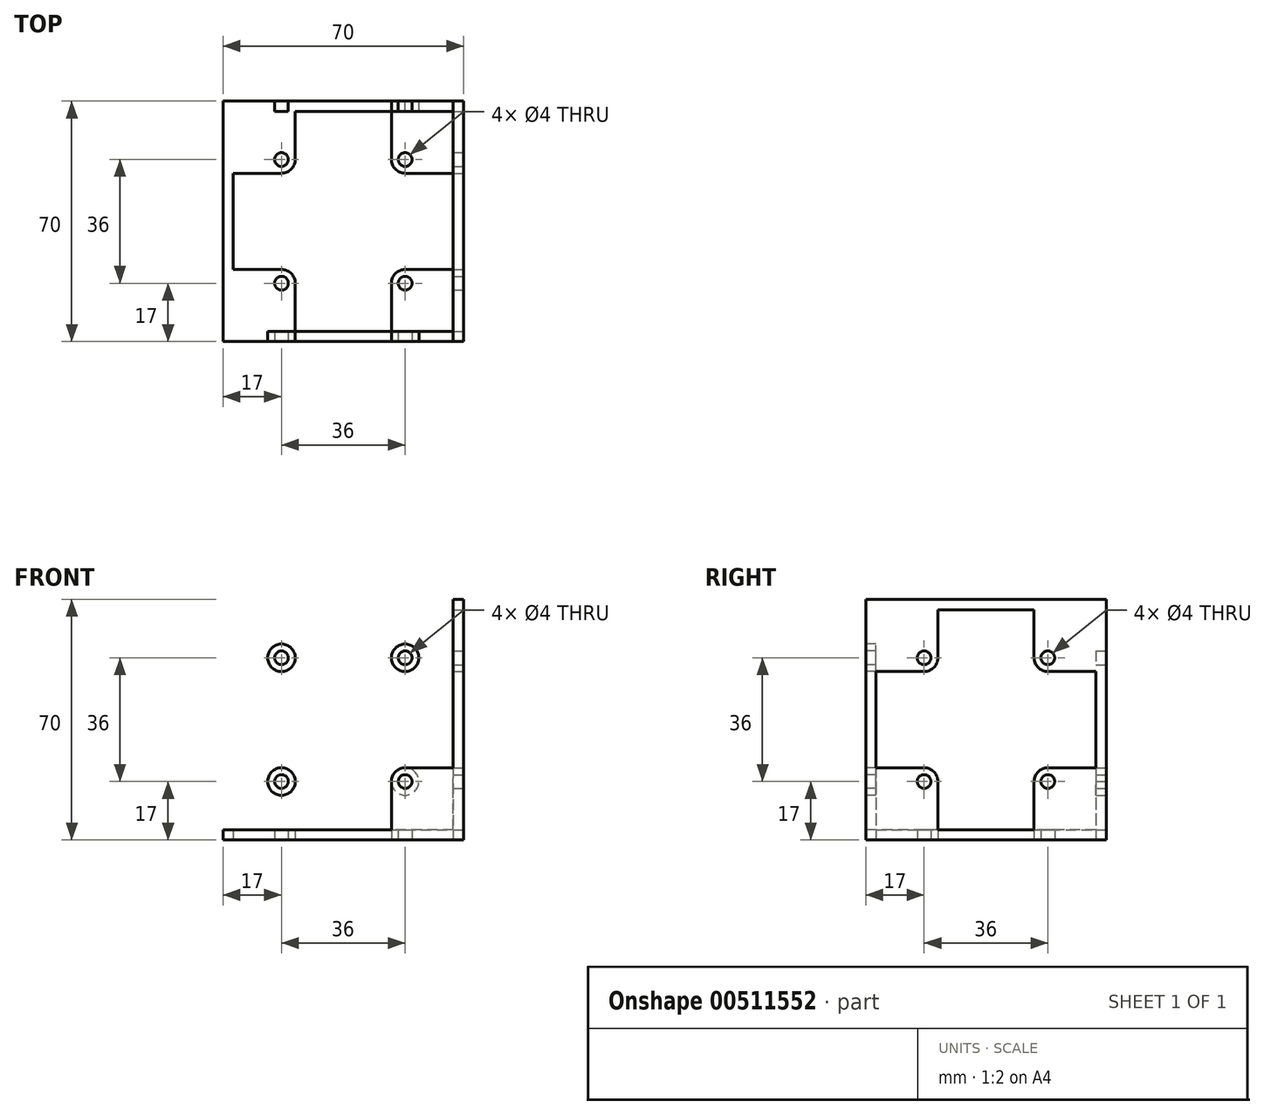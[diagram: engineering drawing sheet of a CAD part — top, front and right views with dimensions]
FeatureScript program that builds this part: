
annotation { "Feature Type Name" : "Feature", "Feature Type Description" : "" }
export const myFeature = defineFeature(function(context is Context, id is Id, definition is map)
    precondition{}
    {
        {
            var Q0;
            Q0=qCreatedBy(makeId("Front.planeOp"),FACE);
            var sketch = newSketch(context, id + "F0", { "sketchPlane" : qUnion([Q0])});
            skLineSegment(sketch, "E0", {"start": v(-35, 0) * mm, "end": v(-35, 35) * mm});
            skLineSegment(sketch, "E1", {"start": v(-35, 35) * mm, "end": v(35, 35) * mm});
            skLineSegment(sketch, "E2", {"start": v(35, 35) * mm, "end": v(35, 0) * mm});
            skLineSegment(sketch, "E3", {"start": v(35, 0) * mm, "end": v(35, -35) * mm});
            skLineSegment(sketch, "E4", {"start": v(35, -35) * mm, "end": v(-35, -35) * mm});
            skLineSegment(sketch, "E5", {"start": v(-35, -35) * mm, "end": v(-35, 0) * mm});
            skLineSegment(sketch, "E6", {"start": v(-32, 32) * mm, "end": v(32, 32) * mm});
            skLineSegment(sketch, "E7", {"start": v(32, 32) * mm, "end": v(32, -32) * mm});
            skLineSegment(sketch, "E8", {"start": v(32, -32) * mm, "end": v(-32, -32) * mm});
            skLineSegment(sketch, "E9", {"start": v(-32, -32) * mm, "end": v(-32, 32) * mm});
            skLineSegment(sketch, "E10", {"start": v(-18, -14) * mm, "end": v(-32, -14) * mm});
            skLineSegment(sketch, "E11", {"start": v(32, 14) * mm, "end": v(18, 14) * mm});
            skLineSegment(sketch, "E12", {"start": v(18, -14) * mm, "end": v(32, -14) * mm});
            skLineSegment(sketch, "E13", {"start": v(14, 32) * mm, "end": v(14, 18) * mm});
            skLineSegment(sketch, "E14", {"start": v(-14, -18) * mm, "end": v(-14, -32) * mm});
            skLineSegment(sketch, "E15", {"start": v(14, -18) * mm, "end": v(14, -32) * mm});
            skLineSegment(sketch, "E16", {"start": v(-14, 18) * mm, "end": v(-14, 32) * mm});
            skLineSegment(sketch, "E17", {"start": v(-18, 14) * mm, "end": v(-32, 14) * mm});
            skCircle(sketch, "E18", {"center": v(-18, 18) * mm, "radius": 2 * mm});
            skCircle(sketch, "E19", {"center": v(-18, 18) * mm, "radius": 4 * mm});
            skPoint(sketch, "E20.visualSharp", {"position": v(-14, 14) * mm});
            skArc(sketch, "E20.filletArc", {"start": v(-18, 14) * mm, "mid": v(-15.17, 15.17) * mm, "end": v(-14, 18) * mm});
            skCircle(sketch, "E21", {"center": v(18, 18) * mm, "radius": 2 * mm});
            skCircle(sketch, "E22", {"center": v(18, 18) * mm, "radius": 4 * mm});
            skCircle(sketch, "E23", {"center": v(-18, -18) * mm, "radius": 2 * mm});
            skCircle(sketch, "E24", {"center": v(-18, -18) * mm, "radius": 4 * mm});
            skCircle(sketch, "E25", {"center": v(18, -18) * mm, "radius": 2 * mm});
            skCircle(sketch, "E26", {"center": v(18, -18) * mm, "radius": 4 * mm});
            skLineSegment(sketch, "E27", {"start": v(-32, 32) * mm, "end": v(-35, 32) * mm});
            skLineSegment(sketch, "E28", {"start": v(-35, 32) * mm, "end": v(-32, 32) * mm});
            skLineSegment(sketch, "E29", {"start": v(32, 32) * mm, "end": v(32, 35) * mm});
            skLineSegment(sketch, "E30", {"start": v(32, 32) * mm, "end": v(35, 32) * mm});
            skLineSegment(sketch, "E31", {"start": v(-35, -32) * mm, "end": v(-32, -32) * mm});
            skLineSegment(sketch, "E32", {"start": v(-32, -32) * mm, "end": v(-32, -35) * mm});
            skLineSegment(sketch, "E33", {"start": v(32, -32) * mm, "end": v(32, -35) * mm});
            skLineSegment(sketch, "E34", {"start": v(32, -32) * mm, "end": v(35, -32) * mm});
            skPoint(sketch, "E35.visualSharp", {"position": v(14, 14) * mm});
            skArc(sketch, "E35.filletArc", {"start": v(14, 18) * mm, "mid": v(15.17, 15.17) * mm, "end": v(18, 14) * mm});
            skPoint(sketch, "E36.visualSharp", {"position": v(14, -14) * mm});
            skArc(sketch, "E36.filletArc", {"start": v(18, -14) * mm, "mid": v(15.17, -15.17) * mm, "end": v(14, -18) * mm});
            skPoint(sketch, "E37.visualSharp", {"position": v(-14, -14) * mm});
            skArc(sketch, "E37.filletArc", {"start": v(-14, -18) * mm, "mid": v(-15.17, -15.17) * mm, "end": v(-18, -14) * mm});
            skCircle(sketch, "E38", {"center": v(-18, 18) * mm, "radius": 6 * mm});
            skSolve(sketch);
        }
        {
            var Q0;
            {var subQ3=sQuery(id+"F0.wireOp",EDGE,"E28");Q0=makeQuery(id+"F0.imprint","IMPRINT",FACE,{"disambiguationData":[TD([[makeQuery(id+"F0.imprint","IMPRINT",EDGE,{"derivedFrom":subQ3}),1.0]])]});}
            var Q1;
            {var subQ7=sQuery(id+"F0.wireOp",EDGE,"E30");Q1=makeQuery(id+"F0.imprint","IMPRINT",FACE,{"disambiguationData":[TD([[makeQuery(id+"F0.imprint","IMPRINT",EDGE,{"derivedFrom":subQ7}),-1.0]])]});}
            var Q2;
            {var subQ3=sQuery(id+"F0.wireOp",EDGE,"E29");Q2=makeQuery(id+"F0.imprint","IMPRINT",FACE,{"disambiguationData":[TD([[makeQuery(id+"F0.imprint","IMPRINT",EDGE,{"derivedFrom":subQ3}),-1.0]])]});}
            var Q3;
            {var subQ7=sQuery(id+"F0.wireOp",EDGE,"E28");Q3=makeQuery(id+"F0.imprint","IMPRINT",FACE,{"disambiguationData":[TD([[makeQuery(id+"F0.imprint","IMPRINT",EDGE,{"derivedFrom":subQ7}),-1.0]])]});}
            var Q4;
            {var subQ0=sQuery(id+"F0.wireOp",EDGE,"E32");Q4=makeQuery(id+"F0.imprint","IMPRINT",FACE,{"disambiguationData":[TD([[makeQuery(id+"F0.imprint","IMPRINT",EDGE,{"derivedFrom":subQ0}),1.0]])]});}
            var Q5;
            {var subQ4=sQuery(id+"F0.wireOp",EDGE,"E31");Q5=makeQuery(id+"F0.imprint","IMPRINT",FACE,{"disambiguationData":[TD([[makeQuery(id+"F0.imprint","IMPRINT",EDGE,{"derivedFrom":subQ4}),-1.0]])]});}
            var Q6;
            {var subQ4=sQuery(id+"F0.wireOp",EDGE,"E33");Q6=makeQuery(id+"F0.imprint","IMPRINT",FACE,{"disambiguationData":[TD([[makeQuery(id+"F0.imprint","IMPRINT",EDGE,{"derivedFrom":subQ4}),1.0]])]});}
            extrude(context, id + "F1", {"entities" : qUnion([Q0, Q1, Q2, Q3, Q4, Q5, Q6]), "endBound" : BoundingType.SYMMETRIC, "depth" : 70 * mm, "offsetDistance" : 25 * mm});
        }
        {
            var Q0;
            Q0=makeQuery(id+"F1.opExtrude","CAP_FACE",FACE,{"disambiguationData":[OSD([sQuery(id+"F0.wireOp",EDGE,"E0"),sQuery(id+"F0.wireOp",EDGE,"E1"),sQuery(id+"F0.wireOp",EDGE,"E2"),sQuery(id+"F0.wireOp",EDGE,"E3"),sQuery(id+"F0.wireOp",EDGE,"E4"),sQuery(id+"F0.wireOp",EDGE,"E5"),sQuery(id+"F0.wireOp",EDGE,"E6"),sQuery(id+"F0.wireOp",EDGE,"E7"),sQuery(id+"F0.wireOp",EDGE,"E8"),sQuery(id+"F0.wireOp",EDGE,"E9")])],"isStart":false});
            var sketch = newSketch(context, id + "F2", { "sketchPlane" : qUnion([Q0])});
            skLineSegment(sketch, "E39.0", {"start": v(-18, 14) * mm, "end": v(-32, 14) * mm});
            skLineSegment(sketch, "E39.1", {"start": v(-14, 18) * mm, "end": v(-14, 32) * mm});
            skArc(sketch, "E39.2", {"start": v(-18, 14) * mm, "mid": v(-15.17, 15.17) * mm, "end": v(-14, 18) * mm});
            skCircle(sketch, "E39.3", {"center": v(-18, 18) * mm, "radius": 2 * mm});
            skCircle(sketch, "E39.4", {"center": v(-18, 18) * mm, "radius": 4 * mm});
            skLineSegment(sketch, "E39.5", {"start": v(14, 32) * mm, "end": v(14, 18) * mm});
            skCircle(sketch, "E39.6", {"center": v(18, 18) * mm, "radius": 4 * mm});
            skLineSegment(sketch, "E39.7", {"start": v(32, 14) * mm, "end": v(18, 14) * mm});
            skLineSegment(sketch, "E39.8", {"start": v(18, -14) * mm, "end": v(32, -14) * mm});
            skCircle(sketch, "E39.9", {"center": v(18, -18) * mm, "radius": 4 * mm});
            skCircle(sketch, "E39.10", {"center": v(18, -18) * mm, "radius": 2 * mm});
            skLineSegment(sketch, "E39.11", {"start": v(14, -18) * mm, "end": v(14, -32) * mm});
            skLineSegment(sketch, "E39.12", {"start": v(-14, -18) * mm, "end": v(-14, -32) * mm});
            skCircle(sketch, "E39.13", {"center": v(-18, -18) * mm, "radius": 4 * mm});
            skLineSegment(sketch, "E39.14", {"start": v(-18, -14) * mm, "end": v(-32, -14) * mm});
            skCircle(sketch, "E39.15", {"center": v(-18, -18) * mm, "radius": 2 * mm});
            skCircle(sketch, "E40.0", {"center": v(18, 18) * mm, "radius": 2 * mm});
            skSolve(sketch);
        }
        {
            var Q0;
            {var subQ5=sQuery(id+"F2.wireOp",EDGE,"E39.0");Q0=makeQuery(id+"F2.imprint","IMPRINT",FACE,{"disambiguationData":[TD([[makeQuery(id+"F2.imprint","IMPRINT",EDGE,{"derivedFrom":subQ5}),-1.0]])]});}
            var Q1;
            Q1=makeQuery(id+"F2.imprint","IMPRINT",FACE,{"disambiguationData":[TD([[makeQuery(id+"F2.imprint","IMPRINT",EDGE,{"derivedFrom":sQuery(id+"F2.wireOp",EDGE,"E39.3")}),-1.0]])]});
            var Q2;
            Q2=makeQuery(id+"F2.imprint","IMPRINT",FACE,{"disambiguationData":[TD([[makeQuery(id+"F2.imprint","IMPRINT",EDGE,{"derivedFrom":sQuery(id+"F2.wireOp",EDGE,"E40.0")}),-1.0]])]});
            var Q3;
            {var subQ2=sQuery(id+"F2.wireOp",EDGE,"E39.5");Q3=makeQuery(id+"F2.imprint","IMPRINT",FACE,{"disambiguationData":[TD([[makeQuery(id+"F2.imprint","IMPRINT",EDGE,{"derivedFrom":subQ2}),1.0]])]});}
            var Q4;
            {var subQ3=sQuery(id+"F2.wireOp",EDGE,"E39.8");Q4=makeQuery(id+"F2.imprint","IMPRINT",FACE,{"disambiguationData":[TD([[makeQuery(id+"F2.imprint","IMPRINT",EDGE,{"derivedFrom":subQ3}),-1.0]])]});}
            var Q5;
            Q5=makeQuery(id+"F2.imprint","IMPRINT",FACE,{"disambiguationData":[TD([[makeQuery(id+"F2.imprint","IMPRINT",EDGE,{"derivedFrom":sQuery(id+"F2.wireOp",EDGE,"E39.10")}),-1.0]])]});
            var Q6;
            Q6=makeQuery(id+"F2.imprint","IMPRINT",FACE,{"disambiguationData":[TD([[makeQuery(id+"F2.imprint","IMPRINT",EDGE,{"derivedFrom":sQuery(id+"F2.wireOp",EDGE,"E39.15")}),-1.0]])]});
            var Q7;
            {var subQ4=sQuery(id+"F2.wireOp",EDGE,"E39.12");Q7=makeQuery(id+"F2.imprint","IMPRINT",FACE,{"disambiguationData":[TD([[makeQuery(id+"F2.imprint","IMPRINT",EDGE,{"derivedFrom":subQ4}),-1.0]])]});}
            extrude(context, id + "F3", {"entities" : qUnion([Q0, Q1, Q2, Q3, Q4, Q5, Q6, Q7]), "operationType" : NewBodyOperationType.ADD, "oppositeDirection" : true, "depth" : 3 * mm, "offsetDistance" : 25 * mm});
        }
        {
            var Q0;
            Q0=makeQuery(id+"F1.opExtrude","CAP_FACE",FACE,{"disambiguationData":[OSD([sQuery(id+"F0.wireOp",EDGE,"E0"),sQuery(id+"F0.wireOp",EDGE,"E1"),sQuery(id+"F0.wireOp",EDGE,"E2"),sQuery(id+"F0.wireOp",EDGE,"E3"),sQuery(id+"F0.wireOp",EDGE,"E4"),sQuery(id+"F0.wireOp",EDGE,"E5"),sQuery(id+"F0.wireOp",EDGE,"E6"),sQuery(id+"F0.wireOp",EDGE,"E7"),sQuery(id+"F0.wireOp",EDGE,"E8"),sQuery(id+"F0.wireOp",EDGE,"E9")])],"isStart":true});
            var sketch = newSketch(context, id + "F4", { "sketchPlane" : qUnion([Q0])});
            skLineSegment(sketch, "E41.0", {"start": v(14, 18) * mm, "end": v(14, 32) * mm});
            skArc(sketch, "E41.1", {"start": v(18, 14) * mm, "mid": v(15.17, 15.17) * mm, "end": v(14, 18) * mm});
            skLineSegment(sketch, "E41.2", {"start": v(18, 14) * mm, "end": v(32, 14) * mm});
            skCircle(sketch, "E41.3", {"center": v(18, 18) * mm, "radius": 2 * mm});
            skCircle(sketch, "E41.4", {"center": v(-18, 18) * mm, "radius": 2 * mm});
            skLineSegment(sketch, "E41.5", {"start": v(-32, 14) * mm, "end": v(-18, 14) * mm});
            skLineSegment(sketch, "E41.6", {"start": v(-14, 32) * mm, "end": v(-14, 18) * mm});
            skCircle(sketch, "E41.7", {"center": v(-18, 18) * mm, "radius": 4 * mm});
            skCircle(sketch, "E41.8", {"center": v(18, 18) * mm, "radius": 4 * mm});
            skLineSegment(sketch, "E41.9", {"start": v(-18, -14) * mm, "end": v(-32, -14) * mm});
            skArc(sketch, "E41.10", {"start": v(-18, -14) * mm, "mid": v(-15.17, -15.17) * mm, "end": v(-14, -18) * mm});
            skCircle(sketch, "E41.11", {"center": v(-18, -18) * mm, "radius": 4 * mm});
            skArc(sketch, "E41.12", {"start": v(14, -18) * mm, "mid": v(15.17, -15.17) * mm, "end": v(18, -14) * mm});
            skLineSegment(sketch, "E41.13", {"start": v(18, -14) * mm, "end": v(32, -14) * mm});
            skCircle(sketch, "E41.14", {"center": v(18, -18) * mm, "radius": 4 * mm});
            skCircle(sketch, "E41.15", {"center": v(18, -18) * mm, "radius": 2 * mm});
            skLineSegment(sketch, "E41.16", {"start": v(14, -18) * mm, "end": v(14, -32) * mm});
            skLineSegment(sketch, "E41.17", {"start": v(-14, -18) * mm, "end": v(-14, -32) * mm});
            skCircle(sketch, "E41.18", {"center": v(-18, -18) * mm, "radius": 2 * mm});
            skSolve(sketch);
        }
        {
            var Q0;
            {var subQ1=sQuery(id+"F4.wireOp",EDGE,"E41.5");Q0=makeQuery(id+"F4.imprint","IMPRINT",FACE,{"disambiguationData":[TD([[makeQuery(id+"F4.imprint","IMPRINT",EDGE,{"derivedFrom":subQ1}),1.0]])]});}
            var Q1;
            Q1=makeQuery(id+"F4.imprint","IMPRINT",FACE,{"disambiguationData":[TD([[makeQuery(id+"F4.imprint","IMPRINT",EDGE,{"derivedFrom":sQuery(id+"F4.wireOp",EDGE,"E41.4")}),1.0]])]});
            var Q2;
            {var subQ3=sQuery(id+"F4.wireOp",EDGE,"E41.0");Q2=makeQuery(id+"F4.imprint","IMPRINT",FACE,{"disambiguationData":[TD([[makeQuery(id+"F4.imprint","IMPRINT",EDGE,{"derivedFrom":subQ3}),-1.0]])]});}
            var Q3;
            Q3=makeQuery(id+"F4.imprint","IMPRINT",FACE,{"disambiguationData":[TD([[makeQuery(id+"F4.imprint","IMPRINT",EDGE,{"derivedFrom":sQuery(id+"F4.wireOp",EDGE,"E41.3")}),1.0]])]});
            var Q4;
            {var subQ5=sQuery(id+"F4.wireOp",EDGE,"E41.13");Q4=makeQuery(id+"F4.imprint","IMPRINT",FACE,{"disambiguationData":[TD([[makeQuery(id+"F4.imprint","IMPRINT",EDGE,{"derivedFrom":subQ5}),-1.0]])]});}
            var Q5;
            Q5=makeQuery(id+"F4.imprint","IMPRINT",FACE,{"disambiguationData":[TD([[makeQuery(id+"F4.imprint","IMPRINT",EDGE,{"derivedFrom":sQuery(id+"F4.wireOp",EDGE,"E41.15")}),1.0]])]});
            var Q6;
            Q6=makeQuery(id+"F4.imprint","IMPRINT",FACE,{"disambiguationData":[TD([[makeQuery(id+"F4.imprint","IMPRINT",EDGE,{"derivedFrom":sQuery(id+"F4.wireOp",EDGE,"E41.18")}),1.0]])]});
            var Q7;
            {var subQ3=sQuery(id+"F4.wireOp",EDGE,"E41.9");Q7=makeQuery(id+"F4.imprint","IMPRINT",FACE,{"disambiguationData":[TD([[makeQuery(id+"F4.imprint","IMPRINT",EDGE,{"derivedFrom":subQ3}),1.0]])]});}
            extrude(context, id + "F5", {"entities" : qUnion([Q0, Q1, Q2, Q3, Q4, Q5, Q6, Q7]), "operationType" : NewBodyOperationType.ADD, "oppositeDirection" : true, "depth" : 3 * mm, "offsetDistance" : 25 * mm});
        }
        {
            var Q0;
            Q0=makeQuery(id+"F1.opExtrude","SWEPT_FACE",FACE,{"disambiguationData":[OSD([sQuery(id+"F0.wireOp",EDGE,"E2"),sQuery(id+"F0.wireOp",EDGE,"E3")])]});
            var sketch = newSketch(context, id + "F6", { "sketchPlane" : qUnion([Q0])});
            skLineSegment(sketch, "E42", {"start": v(-35, 32) * mm, "end": v(35, 32) * mm});
            skLineSegment(sketch, "E43", {"start": v(-32, 35) * mm, "end": v(-32, -35) * mm});
            skLineSegment(sketch, "E44", {"start": v(32, 35) * mm, "end": v(32, -35) * mm});
            skLineSegment(sketch, "E45", {"start": v(35, -32) * mm, "end": v(-35, -32) * mm});
            skLineSegment(sketch, "E46", {"start": v(-14, 32) * mm, "end": v(-14, 18) * mm});
            skLineSegment(sketch, "E47", {"start": v(-18, 14) * mm, "end": v(-32, 14) * mm});
            skLineSegment(sketch, "E48", {"start": v(-32, -14) * mm, "end": v(-18, -14) * mm});
            skLineSegment(sketch, "E49", {"start": v(-14, -18) * mm, "end": v(-14, -32) * mm});
            skLineSegment(sketch, "E50", {"start": v(14, -32) * mm, "end": v(14, -18) * mm});
            skLineSegment(sketch, "E51", {"start": v(18, -14) * mm, "end": v(32, -14) * mm});
            skLineSegment(sketch, "E52", {"start": v(14, 32) * mm, "end": v(14, 18) * mm});
            skLineSegment(sketch, "E53", {"start": v(18, 14) * mm, "end": v(32, 14) * mm});
            skCircle(sketch, "E54", {"center": v(-18, 18) * mm, "radius": 2 * mm});
            skCircle(sketch, "E55", {"center": v(-18, 18) * mm, "radius": 4 * mm});
            skCircle(sketch, "E56", {"center": v(18, 18) * mm, "radius": 2 * mm});
            skCircle(sketch, "E57", {"center": v(18, 18) * mm, "radius": 4 * mm});
            skCircle(sketch, "E58", {"center": v(18, -18) * mm, "radius": 2 * mm});
            skCircle(sketch, "E59", {"center": v(18, -18) * mm, "radius": 4 * mm});
            skCircle(sketch, "E60", {"center": v(-18, -18) * mm, "radius": 2 * mm});
            skCircle(sketch, "E61", {"center": v(-18, -18) * mm, "radius": 4 * mm});
            skPoint(sketch, "E62.visualSharp", {"position": v(-14, 14) * mm});
            skArc(sketch, "E62.filletArc", {"start": v(-18, 14) * mm, "mid": v(-15.17, 15.17) * mm, "end": v(-14, 18) * mm});
            skPoint(sketch, "E63.visualSharp", {"position": v(14, 14) * mm});
            skArc(sketch, "E63.filletArc", {"start": v(14, 18) * mm, "mid": v(15.17, 15.17) * mm, "end": v(18, 14) * mm});
            skPoint(sketch, "E64.visualSharp", {"position": v(14, -14) * mm});
            skArc(sketch, "E64.filletArc", {"start": v(18, -14) * mm, "mid": v(15.17, -15.17) * mm, "end": v(14, -18) * mm});
            skPoint(sketch, "E65.visualSharp", {"position": v(-14, -14) * mm});
            skArc(sketch, "E65.filletArc", {"start": v(-14, -18) * mm, "mid": v(-15.17, -15.17) * mm, "end": v(-18, -14) * mm});
            skSolve(sketch);
        }
        {
            var Q0;
            {var subQ1=sQuery(id+"F6.wireOp",EDGE,"E46");Q0=makeQuery(id+"F6.imprint","IMPRINT",FACE,{"disambiguationData":[TD([[makeQuery(id+"F6.imprint","IMPRINT",EDGE,{"derivedFrom":subQ1}),1.0]])]});}
            var Q1;
            Q1=makeQuery(id+"F6.imprint","IMPRINT",FACE,{"disambiguationData":[TD([[makeQuery(id+"F6.imprint","IMPRINT",EDGE,{"derivedFrom":sQuery(id+"F6.wireOp",EDGE,"E54")}),1.0]])]});
            var Q2;
            Q2=makeQuery(id+"F6.imprint","IMPRINT",FACE,{"disambiguationData":[TD([[makeQuery(id+"F6.imprint","IMPRINT",EDGE,{"derivedFrom":sQuery(id+"F6.wireOp",EDGE,"E56")}),1.0]])]});
            var Q3;
            Q3=makeQuery(id+"F6.imprint","IMPRINT",FACE,{"disambiguationData":[TD([[makeQuery(id+"F6.imprint","IMPRINT",EDGE,{"derivedFrom":sQuery(id+"F6.wireOp",EDGE,"E58")}),1.0]])]});
            var Q4;
            Q4=makeQuery(id+"F6.imprint","IMPRINT",FACE,{"disambiguationData":[TD([[makeQuery(id+"F6.imprint","IMPRINT",EDGE,{"derivedFrom":sQuery(id+"F6.wireOp",EDGE,"E60")}),1.0]])]});
            extrude(context, id + "F7", {"entities" : qUnion([Q0, Q1, Q2, Q3, Q4]), "operationType" : NewBodyOperationType.REMOVE, "oppositeDirection" : true, "depth" : 3 * mm, "offsetDistance" : 25 * mm});
        }
        {
            var Q0;
            Q0=makeQuery(id+"F1.opExtrude","SWEPT_FACE",FACE,{"disambiguationData":[OSD([sQuery(id+"F0.wireOp",EDGE,"E0"),sQuery(id+"F0.wireOp",EDGE,"E5")])]});
            var sketch = newSketch(context, id + "F8", { "sketchPlane" : qUnion([Q0])});
            skLineSegment(sketch, "E66.0", {"start": v(-18, 14) * mm, "end": v(-32, 14) * mm});
            skLineSegment(sketch, "E66.1", {"start": v(-14, 32) * mm, "end": v(-14, 18) * mm});
            skCircle(sketch, "E66.2", {"center": v(-18, 18) * mm, "radius": 4 * mm});
            skCircle(sketch, "E66.3", {"center": v(-18, 18) * mm, "radius": 2 * mm});
            skLineSegment(sketch, "E66.4", {"start": v(18, 14) * mm, "end": v(32, 14) * mm});
            skCircle(sketch, "E66.5", {"center": v(18, 18) * mm, "radius": 4 * mm});
            skLineSegment(sketch, "E66.6", {"start": v(14, 32) * mm, "end": v(14, 18) * mm});
            skCircle(sketch, "E66.7", {"center": v(18, 18) * mm, "radius": 2 * mm});
            skCircle(sketch, "E66.8", {"center": v(18, -18) * mm, "radius": 4 * mm});
            skLineSegment(sketch, "E66.9", {"start": v(32, -14) * mm, "end": v(18, -14) * mm});
            skCircle(sketch, "E66.10", {"center": v(18, -18) * mm, "radius": 2 * mm});
            skLineSegment(sketch, "E66.11", {"start": v(14, -18) * mm, "end": v(14, -32) * mm});
            skLineSegment(sketch, "E66.12", {"start": v(-14, -32) * mm, "end": v(-14, -18) * mm});
            skCircle(sketch, "E66.13", {"center": v(-18, -18) * mm, "radius": 4 * mm});
            skCircle(sketch, "E66.14", {"center": v(-18, -18) * mm, "radius": 2 * mm});
            skLineSegment(sketch, "E66.15", {"start": v(-18, -14) * mm, "end": v(-32, -14) * mm});
            skLineSegment(sketch, "E67", {"start": v(-14, 32) * mm, "end": v(14, 32) * mm});
            skLineSegment(sketch, "E68", {"start": v(-32, 14) * mm, "end": v(-32, -14) * mm});
            skLineSegment(sketch, "E69", {"start": v(-14, -32) * mm, "end": v(14, -32) * mm});
            skLineSegment(sketch, "E70", {"start": v(32, -14) * mm, "end": v(32, 14) * mm});
            skSolve(sketch);
        }
        {
            var Q0;
            {var subQ7=sQuery(id+"F8.wireOp",EDGE,"E66.0");Q0=makeQuery(id+"F8.imprint","IMPRINT",FACE,{"disambiguationData":[TD([[makeQuery(id+"F8.imprint","IMPRINT",EDGE,{"derivedFrom":subQ7}),1.0]])]});}
            var Q1;
            Q1=makeQuery(id+"F8.imprint","IMPRINT",FACE,{"disambiguationData":[TD([[makeQuery(id+"F8.imprint","IMPRINT",EDGE,{"derivedFrom":sQuery(id+"F8.wireOp",EDGE,"E66.3")}),-1.0]])]});
            var Q2;
            Q2=makeQuery(id+"F8.imprint","IMPRINT",FACE,{"disambiguationData":[TD([[makeQuery(id+"F8.imprint","IMPRINT",EDGE,{"derivedFrom":sQuery(id+"F8.wireOp",EDGE,"E66.7")}),-1.0]])]});
            var Q3;
            Q3=makeQuery(id+"F8.imprint","IMPRINT",FACE,{"disambiguationData":[TD([[makeQuery(id+"F8.imprint","IMPRINT",EDGE,{"derivedFrom":sQuery(id+"F8.wireOp",EDGE,"E66.10")}),-1.0]])]});
            var Q4;
            Q4=makeQuery(id+"F8.imprint","IMPRINT",FACE,{"disambiguationData":[TD([[makeQuery(id+"F8.imprint","IMPRINT",EDGE,{"derivedFrom":sQuery(id+"F8.wireOp",EDGE,"E66.14")}),-1.0]])]});
            extrude(context, id + "F9", {"entities" : qUnion([Q0, Q1, Q2, Q3, Q4]), "operationType" : NewBodyOperationType.REMOVE, "oppositeDirection" : true, "depth" : 3 * mm, "offsetDistance" : 25 * mm});
        }
        {
            var Q0;
            Q0=makeQuery(id+"F1.opExtrude","SWEPT_FACE",FACE,{"disambiguationData":[OSD([sQuery(id+"F0.wireOp",EDGE,"E1")])]});
            var sketch = newSketch(context, id + "F10", { "sketchPlane" : qUnion([Q0])});
            skLineSegment(sketch, "E71", {"start": v(-35, 32) * mm, "end": v(35, 32) * mm});
            skLineSegment(sketch, "E72", {"start": v(32, 35) * mm, "end": v(32, -35) * mm});
            skLineSegment(sketch, "E73", {"start": v(-35, -32) * mm, "end": v(35, -32) * mm});
            skLineSegment(sketch, "E74", {"start": v(-32, 35) * mm, "end": v(-32, -35) * mm});
            skLineSegment(sketch, "E75", {"start": v(-14, 32) * mm, "end": v(-14, 18) * mm});
            skLineSegment(sketch, "E76", {"start": v(-18, 14) * mm, "end": v(-32, 14) * mm});
            skLineSegment(sketch, "E77", {"start": v(14, 32) * mm, "end": v(14, 18) * mm});
            skLineSegment(sketch, "E78", {"start": v(18, 14) * mm, "end": v(32, 14) * mm});
            skLineSegment(sketch, "E79", {"start": v(-32, -14) * mm, "end": v(-18, -14) * mm});
            skLineSegment(sketch, "E80", {"start": v(-14, -18) * mm, "end": v(-14, -32) * mm});
            skLineSegment(sketch, "E81", {"start": v(32, -14) * mm, "end": v(18, -14) * mm});
            skLineSegment(sketch, "E82", {"start": v(14, -18) * mm, "end": v(14, -32) * mm});
            skCircle(sketch, "E83", {"center": v(-18, 18) * mm, "radius": 2 * mm});
            skCircle(sketch, "E84", {"center": v(-18, 18) * mm, "radius": 4 * mm});
            skCircle(sketch, "E85", {"center": v(18, 18) * mm, "radius": 2 * mm});
            skCircle(sketch, "E86", {"center": v(18, 18) * mm, "radius": 4 * mm});
            skCircle(sketch, "E87", {"center": v(-18, -18) * mm, "radius": 2 * mm});
            skCircle(sketch, "E88", {"center": v(-18, -18) * mm, "radius": 4 * mm});
            skCircle(sketch, "E89", {"center": v(18, -18) * mm, "radius": 2 * mm});
            skCircle(sketch, "E90", {"center": v(18, -18) * mm, "radius": 4 * mm});
            skPoint(sketch, "E91.visualSharp", {"position": v(-14, 14) * mm});
            skArc(sketch, "E91.filletArc", {"start": v(-18, 14) * mm, "mid": v(-15.17, 15.17) * mm, "end": v(-14, 18) * mm});
            skPoint(sketch, "E92.visualSharp", {"position": v(14, 14) * mm});
            skArc(sketch, "E92.filletArc", {"start": v(14, 18) * mm, "mid": v(15.17, 15.17) * mm, "end": v(18, 14) * mm});
            skPoint(sketch, "E93.visualSharp", {"position": v(14, -14) * mm});
            skArc(sketch, "E93.filletArc", {"start": v(18, -14) * mm, "mid": v(15.17, -15.17) * mm, "end": v(14, -18) * mm});
            skPoint(sketch, "E94.visualSharp", {"position": v(-14, -14) * mm});
            skArc(sketch, "E94.filletArc", {"start": v(-14, -18) * mm, "mid": v(-15.17, -15.17) * mm, "end": v(-18, -14) * mm});
            skLineSegment(sketch, "E95", {"start": v(-32, 14) * mm, "end": v(-32, -14) * mm});
            skLineSegment(sketch, "E96", {"start": v(-14, -32) * mm, "end": v(14, -32) * mm});
            skLineSegment(sketch, "E97", {"start": v(32, -14) * mm, "end": v(32, 14) * mm});
            skLineSegment(sketch, "E98", {"start": v(14, 32) * mm, "end": v(-14, 32) * mm});
            skSolve(sketch);
        }
        {
            var Q0;
            {var subQ1=sQuery(id+"F10.wireOp",EDGE,"E75");Q0=makeQuery(id+"F10.imprint","IMPRINT",FACE,{"disambiguationData":[TD([[makeQuery(id+"F10.imprint","IMPRINT",EDGE,{"derivedFrom":subQ1}),1.0]])]});}
            var Q1;
            Q1=makeQuery(id+"F10.imprint","IMPRINT",FACE,{"disambiguationData":[TD([[makeQuery(id+"F10.imprint","IMPRINT",EDGE,{"derivedFrom":sQuery(id+"F10.wireOp",EDGE,"E83")}),1.0]])]});
            var Q2;
            Q2=makeQuery(id+"F10.imprint","IMPRINT",FACE,{"disambiguationData":[TD([[makeQuery(id+"F10.imprint","IMPRINT",EDGE,{"derivedFrom":sQuery(id+"F10.wireOp",EDGE,"E85")}),1.0]])]});
            var Q3;
            Q3=makeQuery(id+"F10.imprint","IMPRINT",FACE,{"disambiguationData":[TD([[makeQuery(id+"F10.imprint","IMPRINT",EDGE,{"derivedFrom":sQuery(id+"F10.wireOp",EDGE,"E89")}),1.0]])]});
            var Q4;
            Q4=makeQuery(id+"F10.imprint","IMPRINT",FACE,{"disambiguationData":[TD([[makeQuery(id+"F10.imprint","IMPRINT",EDGE,{"derivedFrom":sQuery(id+"F10.wireOp",EDGE,"E87")}),1.0]])]});
            extrude(context, id + "F11", {"entities" : qUnion([Q0, Q1, Q2, Q3, Q4]), "operationType" : NewBodyOperationType.REMOVE, "oppositeDirection" : true, "depth" : 3 * mm, "offsetDistance" : 25 * mm});
        }
        {
            var Q0;
            Q0=makeQuery(id+"F1.opExtrude","SWEPT_FACE",FACE,{"disambiguationData":[OSD([sQuery(id+"F0.wireOp",EDGE,"E4")])]});
            var sketch = newSketch(context, id + "F12", { "sketchPlane" : qUnion([Q0])});
            skLineSegment(sketch, "E99", {"start": v(-35, 32) * mm, "end": v(35, 32) * mm});
            skLineSegment(sketch, "E100", {"start": v(-35, -32) * mm, "end": v(35, -32) * mm});
            skLineSegment(sketch, "E101", {"start": v(-32, 35) * mm, "end": v(-32, -35) * mm});
            skLineSegment(sketch, "E102", {"start": v(32, 35) * mm, "end": v(32, -35) * mm});
            skLineSegment(sketch, "E103", {"start": v(-32, 14) * mm, "end": v(-18, 14) * mm});
            skLineSegment(sketch, "E104", {"start": v(-14, 18) * mm, "end": v(-14, 32) * mm});
            skLineSegment(sketch, "E105", {"start": v(14, 32) * mm, "end": v(14, 18) * mm});
            skLineSegment(sketch, "E106", {"start": v(18, 14) * mm, "end": v(32, 14) * mm});
            skLineSegment(sketch, "E107", {"start": v(32, 14) * mm, "end": v(32, -14) * mm});
            skLineSegment(sketch, "E108", {"start": v(32, -14) * mm, "end": v(18, -14) * mm});
            skLineSegment(sketch, "E109", {"start": v(14, -18) * mm, "end": v(14, -32) * mm});
            skLineSegment(sketch, "E110", {"start": v(14, -32) * mm, "end": v(-14, -32) * mm});
            skLineSegment(sketch, "E111", {"start": v(-14, -32) * mm, "end": v(-14, -18) * mm});
            skLineSegment(sketch, "E112", {"start": v(-18, -14) * mm, "end": v(-32, -14) * mm});
            skLineSegment(sketch, "E113", {"start": v(-32, -14) * mm, "end": v(-32, 14) * mm});
            skPoint(sketch, "E114.visualSharp", {"position": v(-14, 14) * mm});
            skArc(sketch, "E114.filletArc", {"start": v(-18, 14) * mm, "mid": v(-15.17, 15.17) * mm, "end": v(-14, 18) * mm});
            skPoint(sketch, "E115.visualSharp", {"position": v(14, 14) * mm});
            skArc(sketch, "E115.filletArc", {"start": v(14, 18) * mm, "mid": v(15.17, 15.17) * mm, "end": v(18, 14) * mm});
            skPoint(sketch, "E116.visualSharp", {"position": v(14, -14) * mm});
            skArc(sketch, "E116.filletArc", {"start": v(18, -14) * mm, "mid": v(15.17, -15.17) * mm, "end": v(14, -18) * mm});
            skPoint(sketch, "E117.visualSharp", {"position": v(-14, -14) * mm});
            skArc(sketch, "E117.filletArc", {"start": v(-14, -18) * mm, "mid": v(-15.17, -15.17) * mm, "end": v(-18, -14) * mm});
            skCircle(sketch, "E118", {"center": v(-18, 18) * mm, "radius": 2 * mm});
            skCircle(sketch, "E119", {"center": v(18, 18) * mm, "radius": 2 * mm});
            skCircle(sketch, "E120", {"center": v(18, -18) * mm, "radius": 2 * mm});
            skCircle(sketch, "E121", {"center": v(-18, -18) * mm, "radius": 2 * mm});
            skSolve(sketch);
        }
        {
            var Q0;
            Q0=makeQuery(id+"F12.imprint","IMPRINT",FACE,{"disambiguationData":[TD([[makeQuery(id+"F12.imprint","IMPRINT",EDGE,{"derivedFrom":sQuery(id+"F12.wireOp",EDGE,"E103")}),-1.0]])]});
            var Q1;
            Q1=makeQuery(id+"F12.imprint","IMPRINT",FACE,{"disambiguationData":[TD([[makeQuery(id+"F12.imprint","IMPRINT",EDGE,{"derivedFrom":sQuery(id+"F12.wireOp",EDGE,"E118")}),1.0]])]});
            var Q2;
            Q2=makeQuery(id+"F12.imprint","IMPRINT",FACE,{"disambiguationData":[TD([[makeQuery(id+"F12.imprint","IMPRINT",EDGE,{"derivedFrom":sQuery(id+"F12.wireOp",EDGE,"E121")}),1.0]])]});
            var Q3;
            Q3=makeQuery(id+"F12.imprint","IMPRINT",FACE,{"disambiguationData":[TD([[makeQuery(id+"F12.imprint","IMPRINT",EDGE,{"derivedFrom":sQuery(id+"F12.wireOp",EDGE,"E120")}),1.0]])]});
            var Q4;
            Q4=makeQuery(id+"F12.imprint","IMPRINT",FACE,{"disambiguationData":[TD([[makeQuery(id+"F12.imprint","IMPRINT",EDGE,{"derivedFrom":sQuery(id+"F12.wireOp",EDGE,"E119")}),1.0]])]});
            extrude(context, id + "F13", {"entities" : qUnion([Q0, Q1, Q2, Q3, Q4]), "operationType" : NewBodyOperationType.REMOVE, "oppositeDirection" : true, "depth" : 3 * mm, "offsetDistance" : 25 * mm});
        }
    });
